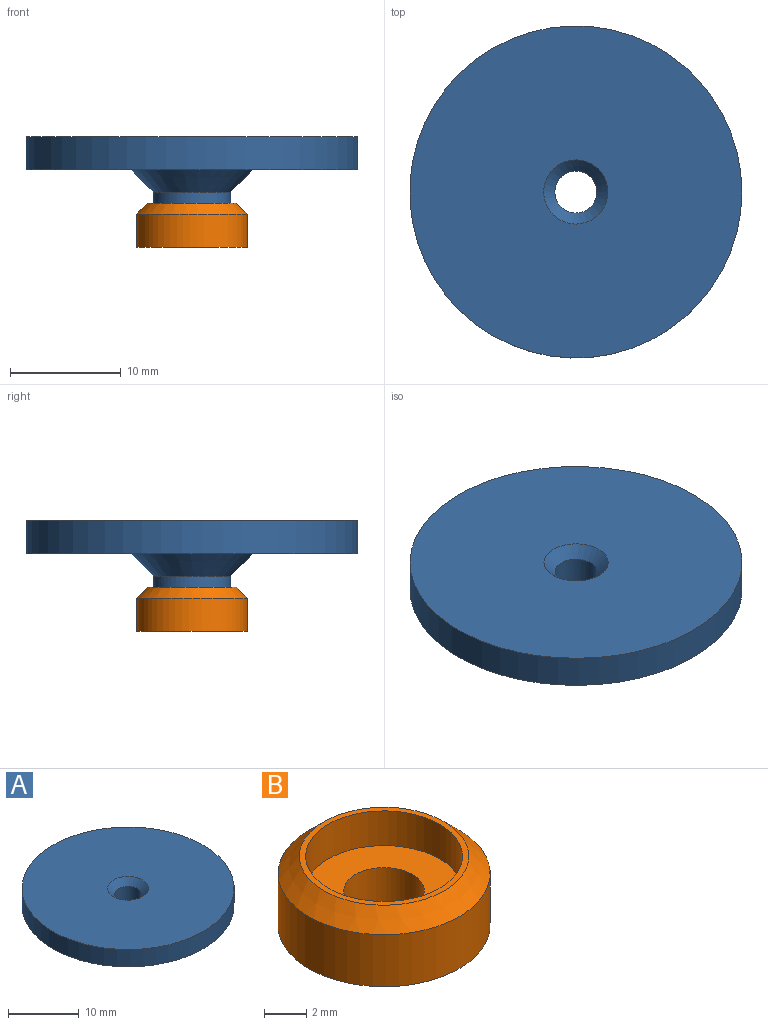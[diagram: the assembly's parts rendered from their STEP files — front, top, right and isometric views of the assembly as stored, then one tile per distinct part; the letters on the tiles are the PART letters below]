
ASSEMBLY  parts=2 mates=1
PART A: 8 faces, bbox 30x30x8 mm
  f0: cylinder r=1.9mm len=7mm, axis (0,0,-1), area 83.6mm2, adj f4,f6
  f1: cylinder r=15mm len=30mm, axis (0,0,-1), area 282.7mm2, adj f2,f3
  f2: plane 30x30mm, normal (0,0,1), area 680.4mm2, adj f1,f4
  f3: plane 30x30mm, normal (0,0,-1), area 611.8mm2, adj f1,f7
  f4: cone r=1.9mm half-angle=45deg, axis (0,0,1), area 21.3mm2, adj f0,f2
  f5: cylinder r=3.5mm len=7mm, axis (0,0,1), area 66mm2, adj f6,f7
  f6: plane 7x7mm, normal (0,0,-1), area 27.1mm2, adj f0,f5
  f7: cone r=3.5mm half-angle=45deg, axis (0,0,1), area 80mm2, adj f3,f5
PART B: 7 faces, bbox 10x10x4 mm
  f0: cylinder r=3.7mm len=7.4mm, axis (0,0,-1), area 46.5mm2, adj f4,f5
  f1: cylinder r=5mm len=10mm, axis (0,0,-1), area 94.2mm2, adj f2,f6
  f2: plane 10x10mm, normal (0,0,-1), area 67.2mm2, adj f1,f3
  f3: cylinder r=1.9mm len=3.8mm, axis (0,0,-1), area 23.9mm2, adj f2,f4
  f4: plane 7.4x7.4mm, normal (0,0,1), area 31.7mm2, adj f0,f3
  f5: plane 8x8mm, normal (0,0,1), area 7.3mm2, adj f0,f6
  f6: cone r=4mm half-angle=45deg, axis (0,0,-1), area 40mm2, adj f1,f5
PLACE A t=(3.75,-3.15,-0.97)mm
PLACE B t=(3.75,-3.15,-7.97)mm fixed
MATE fastened A.f5 <-> B.f3  axis (0,0,-1) through (3.75,-3.15,-5.97)mm
